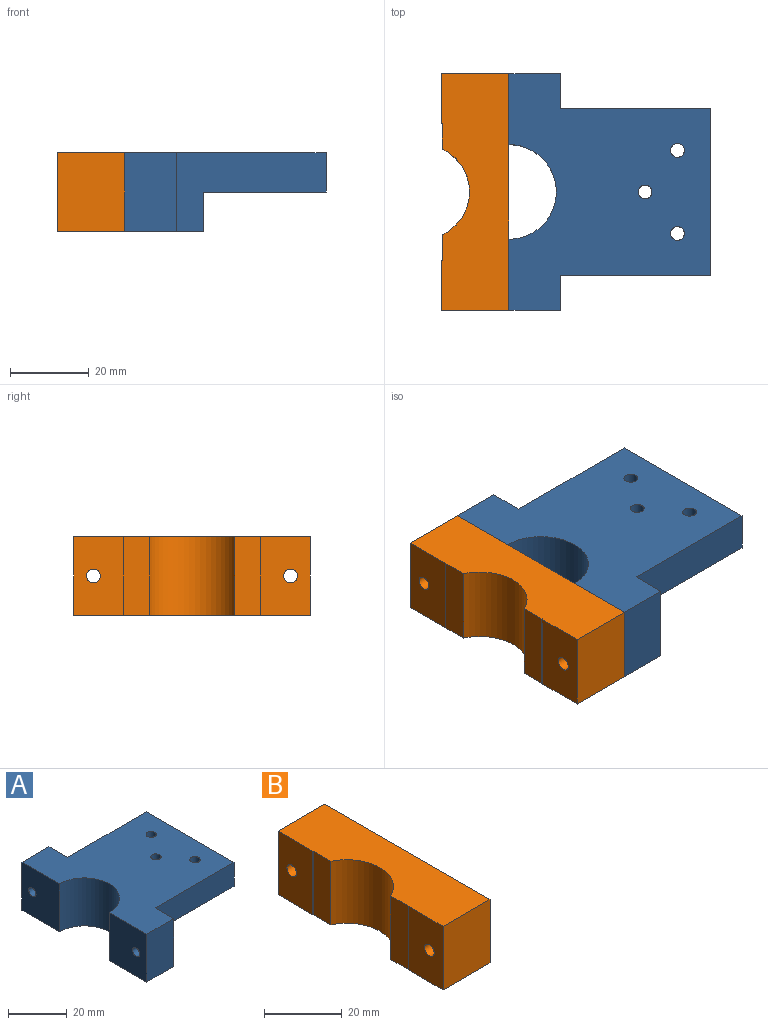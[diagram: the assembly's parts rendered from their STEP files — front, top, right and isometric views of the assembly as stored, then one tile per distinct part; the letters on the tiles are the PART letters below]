
ASSEMBLY  parts=2 mates=1
PART A: 19 faces, bbox 51x60x20 mm
  f0: plane 42.16x31mm, normal (0,0,-1), area 1278mm2, adj f7,f8,f9,f10,f11,f12,f17
  f1: plane 20x18mm, normal (-1,0,0), area 350.4mm2, adj f4,f5,f6,f15,f18
  f2: plane 20x18mm, normal (-1,0,0), area 350.4mm2, adj f3,f5,f6,f16,f18
  f3: plane 20x13mm, normal (0,-1,0), area 260mm2, adj f2,f5,f6,f13
  f4: plane 20x13mm, normal (0,1,0), area 260mm2, adj f1,f5,f6,f14
  f5: plane 60x51mm, normal (0,0,1), area 2126.9mm2, adj f1,f2,f3,f4,f7,f8,f9,f10
  f6: plane 60x20mm, normal (0,0,-1), area 848.9mm2, adj f1,f2,f3,f4,f7,f8,f13,f14
  f7: plane 38x20mm, normal (0,1,0), area 450mm2, adj f0,f5,f6,f9,f14,f17
  f8: plane 38x20mm, normal (0,-1,0), area 450mm2, adj f0,f5,f6,f9,f13,f17
  f9: plane 42.16x10mm, normal (1,0,0), area 421.6mm2, adj f0,f5,f7,f8
  f10: cylinder r=1.75mm len=10mm, axis (0,0,1), area 110mm2, adj f0,f5
  f11: cylinder r=1.75mm len=10mm, axis (0,0,1), area 110mm2, adj f0,f5
  f12: cylinder r=1.75mm len=10mm, axis (0,0,1), area 110mm2, adj f0,f5
  f13: plane 20x8.92mm, normal (1,0,0), area 168.8mm2, adj f3,f5,f6,f8,f16
  f14: plane 20x8.92mm, normal (1,0,0), area 168.8mm2, adj f4,f5,f6,f7,f15
  f15: cylinder r=1.75mm len=13mm, axis (-1,0,0), area 142.9mm2, adj f1,f14
  f16: cylinder r=1.75mm len=13mm, axis (-1,0,0), area 142.9mm2, adj f2,f13
  f17: plane 42.16x10mm, normal (1,0,0), area 421.6mm2, adj f0,f6,f7,f8
  f18: cylinder r=12mm len=24mm, axis (0,0,1), area 754mm2, adj f1,f2,f5,f6
PART B: 14 faces, bbox 17x60x20 mm
  f0: cylinder r=18mm len=20mm, axis (0,0,-1), area 2.1mm2, adj f4,f7,f8,f11
  f1: plane 20x17mm, normal (0,1,0), area 340mm2, adj f2,f6,f7,f8
  f2: plane 20x12.71mm, normal (-1,0,0), area 244.5mm2, adj f1,f3,f7,f8,f9
  f3: cylinder r=18mm len=20mm, axis (0,0,-1), area 2.1mm2, adj f2,f7,f8,f12
  f4: plane 20x12.71mm, normal (-1,0,0), area 244.5mm2, adj f0,f5,f7,f8,f10
  f5: plane 20x17mm, normal (0,-1,0), area 340mm2, adj f4,f6,f7,f8
  f6: plane 60x20mm, normal (1,0,0), area 1180.8mm2, adj f1,f5,f7,f8,f9,f10
  f7: plane 60x17mm, normal (0,0,1), area 909mm2, adj f0,f1,f2,f3,f4,f5,f6,f11
  f8: plane 60x17mm, normal (0,0,-1), area 909mm2, adj f0,f1,f2,f3,f4,f5,f6,f11
  f9: cylinder r=1.75mm len=17mm, axis (-1,0,0), area 186.9mm2, adj f2,f6
  f10: cylinder r=1.75mm len=17mm, axis (-1,0,0), area 186.9mm2, adj f4,f6
  f11: plane 20x6.4mm, normal (-1,0,0), area 128mm2, adj f0,f7,f8,f13
  f12: plane 20x6.4mm, normal (-1,0,0), area 128mm2, adj f3,f7,f8,f13
  f13: cylinder r=12mm len=21.73mm, axis (0,0,-1), area 543.3mm2, adj f7,f8,f11,f12
PLACE A t=(9.04,18.91,-11.55)mm
PLACE B t=(-12.96,18.91,-11.55)mm
MATE fastened B.f10 <-> A.f16  axis (1,0,0) through (9.04,-6.09,-1.55)mm
